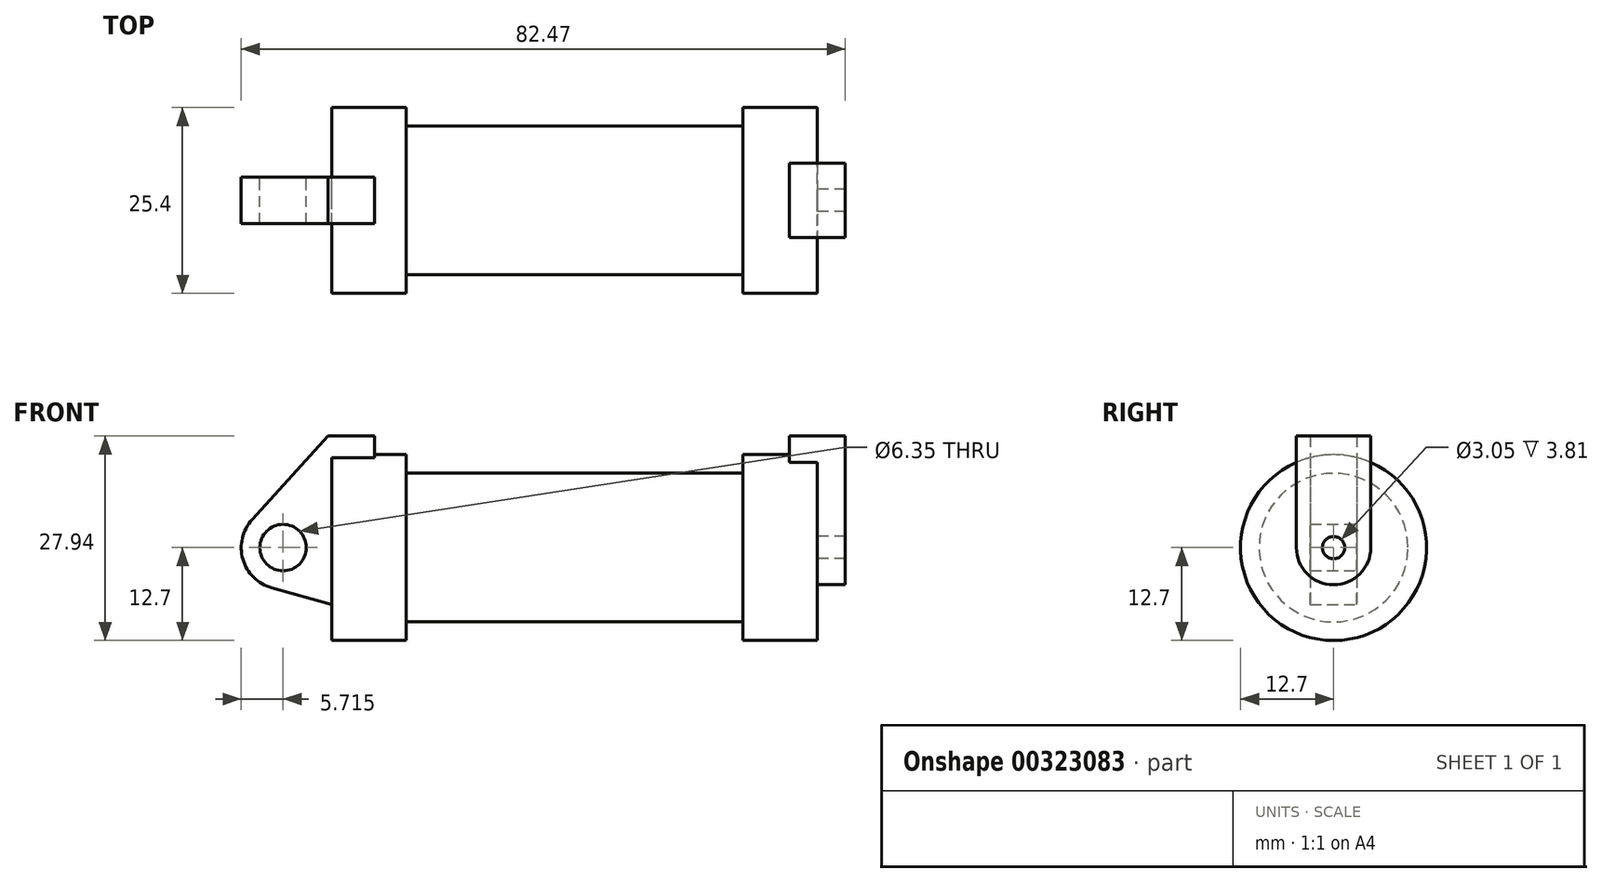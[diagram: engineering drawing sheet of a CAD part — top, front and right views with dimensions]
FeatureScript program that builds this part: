
annotation { "Feature Type Name" : "Feature", "Feature Type Description" : "" }
export const myFeature = defineFeature(function(context is Context, id is Id, definition is map)
    precondition{}
    {
        {
            var Q0;
            Q0=qCreatedBy(makeId("Front.planeOp"),FACE);
            var sketch = newSketch(context, id + "F0", { "sketchPlane" : qUnion([Q0])});
            skLineSegment(sketch, "E0", {"start": v(0, 0) * mm, "end": v(0, 12.7) * mm});
            skLineSegment(sketch, "E1", {"start": v(0, 12.7) * mm, "end": v(10.16, 12.7) * mm});
            skLineSegment(sketch, "E2", {"start": v(10.16, 12.7) * mm, "end": v(10.16, 10.16) * mm});
            skLineSegment(sketch, "E3", {"start": v(10.16, 10.16) * mm, "end": v(56.13, 10.16) * mm});
            skLineSegment(sketch, "E4", {"start": v(56.13, 10.16) * mm, "end": v(56.13, 12.7) * mm});
            skLineSegment(sketch, "E5", {"start": v(56.13, 12.7) * mm, "end": v(66.3, 12.7) * mm});
            skLineSegment(sketch, "E6", {"start": v(66.3, 12.7) * mm, "end": v(66.3, 0) * mm});
            skLineSegment(sketch, "E7", {"start": v(66.3, 0) * mm, "end": v(0, 0) * mm});
            skLineSegment(sketch, "E8", {"start": v(5.84, 15.24) * mm, "end": v(-0.5, 15.24) * mm});
            skLineSegment(sketch, "E9", {"start": v(-0.5, 15.24) * mm, "end": v(-10.88, 3.85) * mm});
            skLineSegment(sketch, "E10", {"start": v(0, 0) * mm, "end": v(-6.65, 0) * mm});
            skCircle(sketch, "E11", {"center": v(-6.65, 0) * mm, "radius": 5.72 * mm});
            skCircle(sketch, "E12", {"center": v(-6.65, 0) * mm, "radius": 3.18 * mm});
            skLineSegment(sketch, "E13", {"start": v(5.84, 15.24) * mm, "end": v(5.84, -9.4) * mm});
            skLineSegment(sketch, "E14", {"start": v(5.84, -9.4) * mm, "end": v(-8.18, -5.5) * mm});
            skSolve(sketch);
        }
        {
            var Q0;
            {var subQ0=sQuery(id+"F0.wireOp",EDGE,"E2");Q0=makeQuery(id+"F0.imprint","IMPRINT",FACE,{"disambiguationData":[TD([[makeQuery(id+"F0.imprint","IMPRINT",EDGE,{"derivedFrom":subQ0}),-1.0]])]});}
            var Q1;
            {var subQ0=sQuery(id+"F0.wireOp",EDGE,"E0");Q1=makeQuery(id+"F0.imprint","IMPRINT",FACE,{"disambiguationData":[TD([[makeQuery(id+"F0.imprint","IMPRINT",EDGE,{"derivedFrom":subQ0}),-1.0]])]});}
            var Q2;
            Q2=sQuery(id+"F0.wireOp",EDGE,"E7");
            revolve(context, id + "F1", {"entities" : qUnion([Q0, Q1]), "axis" : qUnion([Q2]), "revolveType" : RevolveType.FULL});
        }
        {
            var Q0;
            {var subQ0=sQuery(id+"F0.wireOp",EDGE,"E0");Q0=makeQuery(id+"F0.imprint","IMPRINT",FACE,{"disambiguationData":[TD([[makeQuery(id+"F0.imprint","IMPRINT",EDGE,{"derivedFrom":subQ0}),-1.0]])]});}
            var Q1;
            {var subQ1=sQuery(id+"F0.wireOp",EDGE,"E0");Q1=makeQuery(id+"F0.imprint","IMPRINT",FACE,{"disambiguationData":[TD([[makeQuery(id+"F0.imprint","IMPRINT",EDGE,{"derivedFrom":subQ1}),1.0]])]});}
            var Q2;
            {var subQ0=sQuery(id+"F0.wireOp",EDGE,"E14");Q2=makeQuery(id+"F0.imprint","IMPRINT",FACE,{"disambiguationData":[TD([[makeQuery(id+"F0.imprint","IMPRINT",EDGE,{"derivedFrom":subQ0}),-1.0]])]});}
            var Q3;
            {var subQ5=sQuery(id+"F0.wireOp",EDGE,"E12");Q3=makeQuery(id+"F0.imprint","IMPRINT",FACE,{"disambiguationData":[TD([[makeQuery(id+"F0.imprint","IMPRINT",EDGE,{"derivedFrom":subQ5}),-1.0]])]});}
            extrude(context, id + "F2", {"entities" : qUnion([Q0, Q1, Q2, Q3]), "operationType" : NewBodyOperationType.ADD, "endBound" : BoundingType.SYMMETRIC, "depth" : 6.35 * mm});
        }
        {
            var Q0;
            Q0=makeQuery(id+"F1.opRevolve","SWEPT_FACE",FACE,{"disambiguationData":[OSD([sQuery(id+"F0.wireOp",EDGE,"E6")])]});
            var sketch = newSketch(context, id + "F3", { "sketchPlane" : qUnion([Q0])});
            skCircle(sketch, "E15", {"center": v(0, 0) * mm, "radius": 5.08 * mm});
            skCircle(sketch, "E16", {"center": v(0, 0) * mm, "radius": 1.52 * mm});
            skLineSegment(sketch, "E17", {"start": v(5.08, 0) * mm, "end": v(5.08, 15.24) * mm});
            skLineSegment(sketch, "E18", {"start": v(-5.08, 0) * mm, "end": v(-5.08, 15.24) * mm});
            skLineSegment(sketch, "E19", {"start": v(-5.08, 15.24) * mm, "end": v(5.08, 15.24) * mm});
            skSolve(sketch);
        }
        {
            var Q0;
            {var subQ0=sQuery(id+"F3.wireOp",EDGE,"E17");var subQ1=sQuery(id+"F3.wireOp",EDGE,"E15");var subQ2=makeQuery(id+"F3.imprint","INTERSECT",VERTEX,{"derivedFrom":[subQ1,subQ0]});Q0=makeQuery(id+"F3.imprint","IMPRINT",FACE,{"disambiguationData":[TD([[makeQuery(id+"F3.imprint","IMPRINT",EDGE,{"disambiguationData":[TD([[subQ2,-1.0]])],"derivedFrom":subQ1}),-1.0]])]});}
            var Q1;
            Q1=makeQuery(id+"F3.imprint","IMPRINT",FACE,{"disambiguationData":[TD([[makeQuery(id+"F3.imprint","IMPRINT",EDGE,{"derivedFrom":sQuery(id+"F3.wireOp",EDGE,"E16")}),-1.0]])]});
            var Q2;
            {var subQ0=sQuery(id+"F3.wireOp",EDGE,"E19");Q2=makeQuery(id+"F3.imprint","IMPRINT",FACE,{"disambiguationData":[TD([[makeQuery(id+"F3.imprint","IMPRINT",EDGE,{"derivedFrom":subQ0}),-1.0]])]});}
            extrude(context, id + "F4", {"entities" : qUnion([Q0, Q1, Q2]), "operationType" : NewBodyOperationType.ADD, "endBound" : BoundingType.SYMMETRIC, "depth" : 7.62 * mm});
        }
    });
